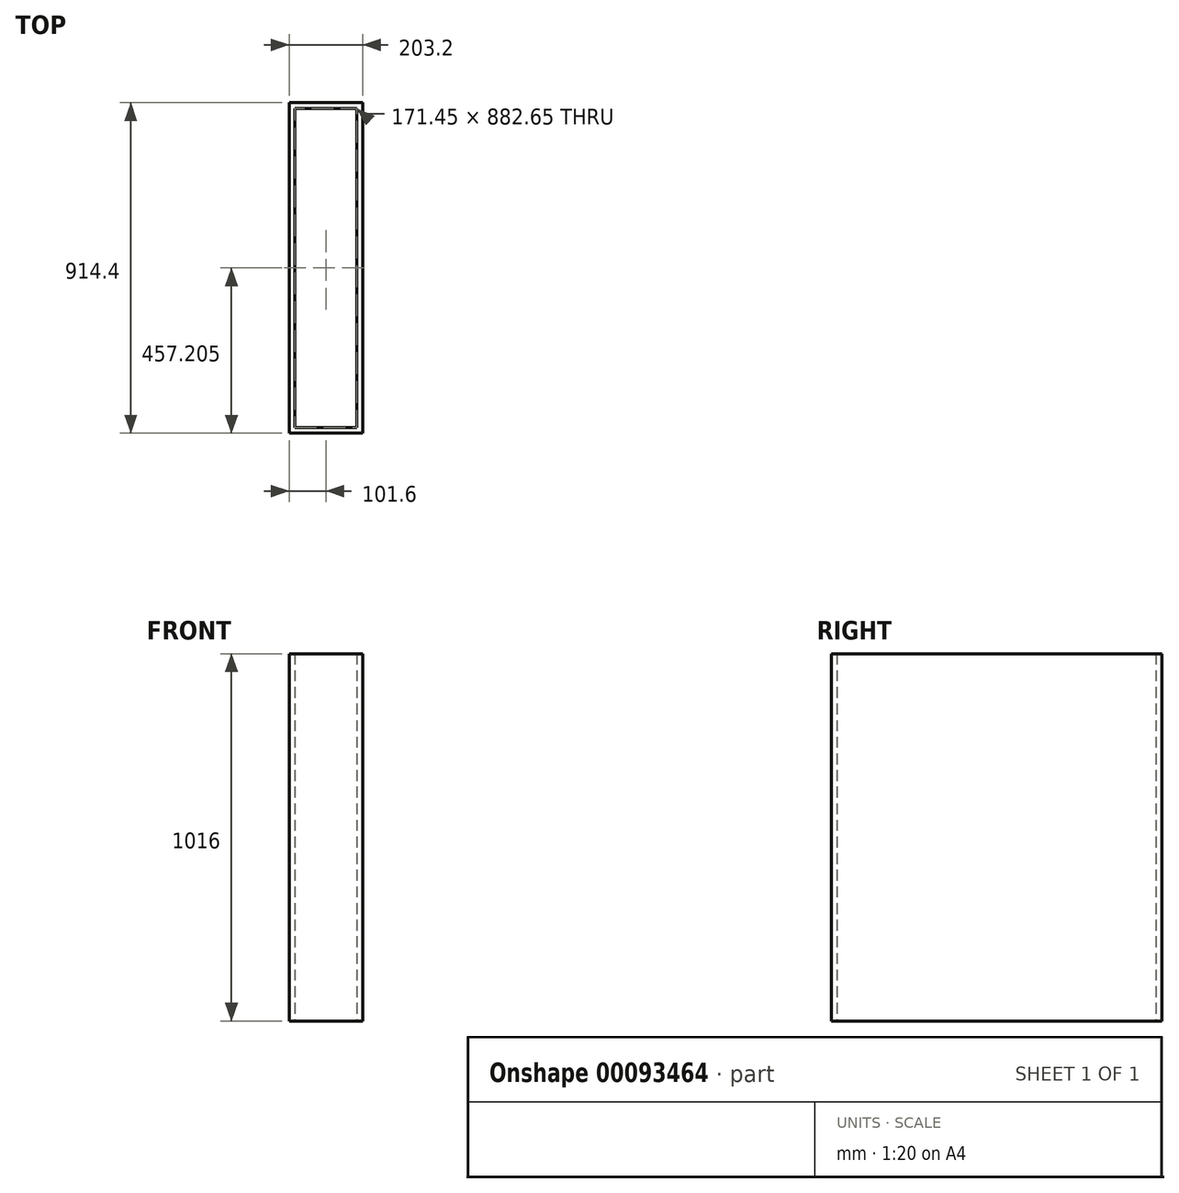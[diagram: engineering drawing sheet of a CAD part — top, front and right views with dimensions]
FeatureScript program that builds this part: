
annotation { "Feature Type Name" : "Feature", "Feature Type Description" : "" }
export const myFeature = defineFeature(function(context is Context, id is Id, definition is map)
    precondition{}
    {
        {
            var Q0;
            Q0=qCreatedBy(makeId("Top.planeOp"),FACE);
            var sketch = newSketch(context, id + "F0", { "sketchPlane" : qUnion([Q0])});
            skLineSegment(sketch, "E0.bottom", {"start": v(33.27, 0) * mm, "end": v(204.72, 0) * mm});
            skLineSegment(sketch, "E0.top", {"start": v(33.27, 882.65) * mm, "end": v(204.72, 882.65) * mm});
            skLineSegment(sketch, "E0.left", {"start": v(33.27, 0) * mm, "end": v(33.27, 882.65) * mm});
            skLineSegment(sketch, "E0.right", {"start": v(204.72, 0) * mm, "end": v(204.72, 882.65) * mm});
            skLineSegment(sketch, "E1.0", {"start": v(220.6, -15.88) * mm, "end": v(220.6, 898.53) * mm});
            skLineSegment(sketch, "E2.0", {"start": v(17.4, 898.53) * mm, "end": v(220.6, 898.53) * mm});
            skLineSegment(sketch, "E3.0", {"start": v(17.4, -15.88) * mm, "end": v(17.4, 898.53) * mm});
            skLineSegment(sketch, "E4.0", {"start": v(17.4, -15.88) * mm, "end": v(220.6, -15.88) * mm});
            skSolve(sketch);
        }
        {
            var Q0;
            Q0=makeQuery(id+"F0.imprint","IMPRINT",FACE,{"disambiguationData":[TD([[makeQuery(id+"F0.imprint","IMPRINT",EDGE,{"derivedFrom":sQuery(id+"F0.wireOp",EDGE,"E0.bottom")}),-1.0]])]});
            extrude(context, id + "F1", {"entities" : qUnion([Q0]), "depth" : 1016 * mm});
        }
    });
